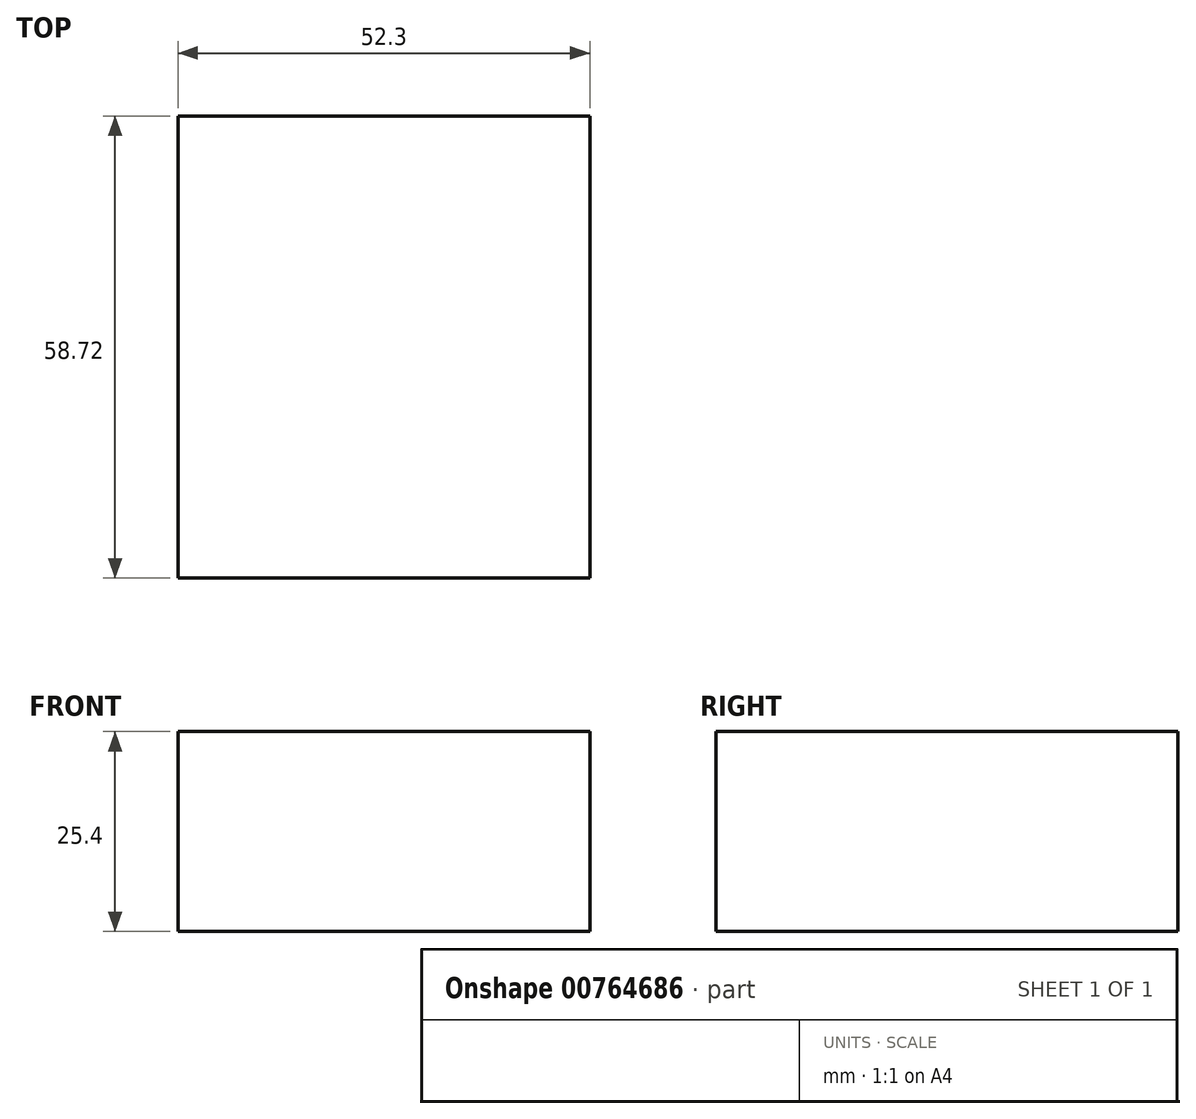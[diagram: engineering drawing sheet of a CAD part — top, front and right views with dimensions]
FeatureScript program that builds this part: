
annotation { "Feature Type Name" : "Feature", "Feature Type Description" : "" }
export const myFeature = defineFeature(function(context is Context, id is Id, definition is map)
    precondition{}
    {
        {
            var Q0;
            Q0=qCreatedBy(makeId("Top.planeOp"),FACE);
            var sketch = newSketch(context, id + "F0", { "sketchPlane" : qUnion([Q0])});
            skLineSegment(sketch, "E0.bottom", {"start": v(26.15, 29.36) * mm, "end": v(-26.15, 29.36) * mm});
            skLineSegment(sketch, "E0.top", {"start": v(26.15, -29.36) * mm, "end": v(-26.15, -29.36) * mm});
            skLineSegment(sketch, "E0.left", {"start": v(26.15, 29.36) * mm, "end": v(26.15, -29.36) * mm});
            skLineSegment(sketch, "E0.right", {"start": v(-26.15, 29.36) * mm, "end": v(-26.15, -29.36) * mm});
            skPoint(sketch, "E0.middle", {"position": v(0, 0) * mm});
            skSolve(sketch);
        }
        {
            var Q0;
            Q0=makeQuery(id+"F0.imprint","IMPRINT",FACE,{"disambiguationData":[TD([[makeQuery(id+"F0.imprint","IMPRINT",EDGE,{"derivedFrom":sQuery(id+"F0.wireOp",EDGE,"E0.bottom")}),1.0]])]});
            extrude(context, id + "F1", {"entities" : qUnion([Q0]), "depth" : 25.4 * mm, "offsetDistance" : 25.4 * mm});
        }
    });
